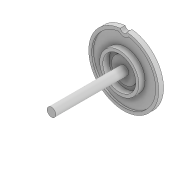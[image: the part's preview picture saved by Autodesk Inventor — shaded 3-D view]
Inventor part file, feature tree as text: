
AUTODESK INVENTOR PART (.ipt)
format: ipt  version: 2020 (Build 240168000, 168)  size: 139,776 bytes
history: native  units: mm
features: extrude x6, sketch x6, plane x3, projected_geometry x1
ambient origin geometry x8: Origin, YZ Plane, XZ Plane, XY Plane, X Axis, Y Axis, Z Axis, Center Point
bodies: Solid1 (feature_tree)
feature tree (16):
  extrude  "Extrusion1"  Depth=1.0mm TaperAngle=0.0deg
  plane  "Work Plane1"
  extrude  "Extrusion3"  Depth=10.75mm
  plane  "Work Plane3"
  extrude  "Extrusion4"  Depth=2.0mm
  plane  "Work Plane2"
  extrude  "Extrusion5"  Depth=24.1mm
  extrude  "Extrusion6"  Depth=0.4mm
  extrude  "Extrusion7"  Depth=1.0mm
  sketch  "Sketch1"  dims[d0=22.8mm d1=1.0mm d2=0.0mm]
  sketch  "Sketch3"  dims[d6=12.75mm d7=10.75mm]
  sketch  "Sketch4"  dims[d8=2.0mm d9=0.0mm d10=2.85mm]
  sketch  "Sketch5"  dims[d11=24.1mm d12=0.0mm d14=8.25mm]
  sketch  "Sketch7"  dims[d15=0.4mm d16=0.0mm d17=2.2mm d18=0.8mm]
  sketch  "Sketch8"  dims[d19=10.0mm d20=0.0mm d21=1.0mm d22=0.57mm d23=0.0mm]
  projected_geometry  "Projected Loop2"
